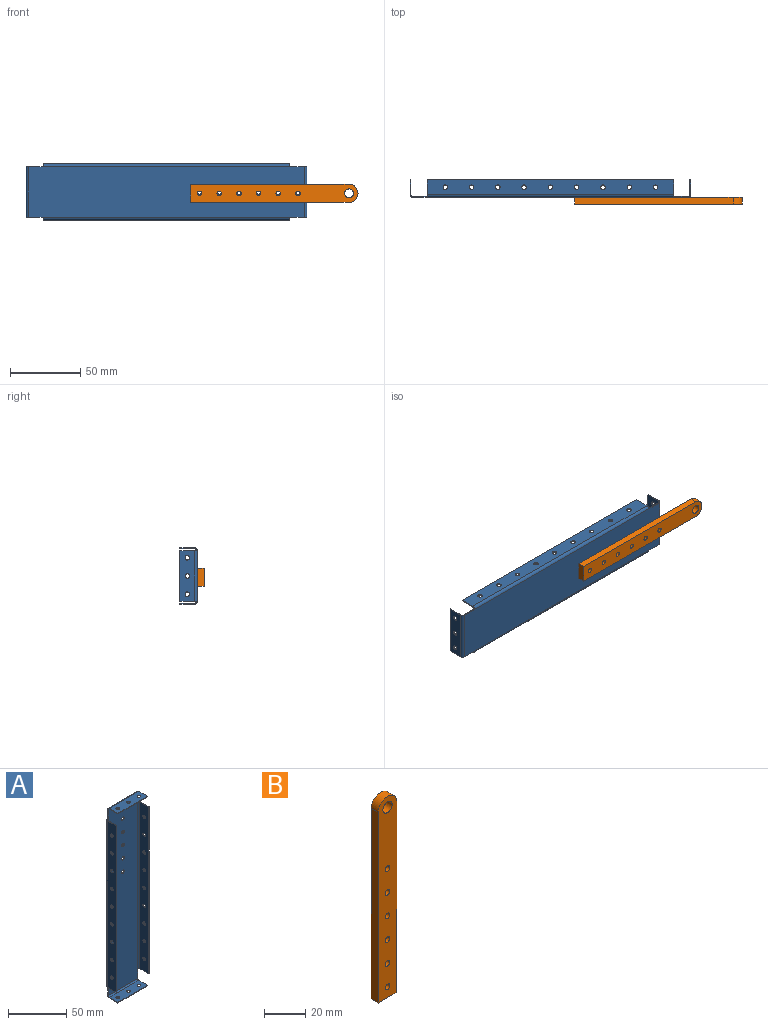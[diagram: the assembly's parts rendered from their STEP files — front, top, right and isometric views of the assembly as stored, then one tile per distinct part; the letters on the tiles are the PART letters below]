
ASSEMBLY  parts=2 mates=2
PART A: 76 faces, bbox 40x12.5x200 mm
  f0: plane 0.64x0mm, normal (0,0,-1), area 0mm2, adj f1,f73
  f1: plane 10.24x0.64mm, normal (1,0,0), area 6.6mm2, adj f0,f14,f15,f36
  f2: plane 10.24x0.64mm, normal (-1,0,0), area 6.6mm2, adj f3,f14,f15,f37
  f3: plane 0.64x0mm, normal (0,0,-1), area 0mm2, adj f2,f54
  f4: plane 0.64x0mm, normal (0,0,1), area 0mm2, adj f5,f55
  f5: plane 10.24x0.64mm, normal (-1,0,0), area 6.6mm2, adj f4,f14,f15,f24
  f6: plane 10.24x0.64mm, normal (1,0,0), area 6.6mm2, adj f8,f14,f15,f25
  f7: cylinder r=1.6mm len=3.2mm, axis (0,-1,0), area 6.4mm2, adj f14,f15
  f8: plane 0.64x0mm, normal (0,0,1), area 0mm2, adj f6,f72
  f9: cylinder r=1.6mm len=3.2mm, axis (0,-1,0), area 6.4mm2, adj f14,f15
  f10: cylinder r=1.6mm len=3.2mm, axis (0,-1,0), area 6.4mm2, adj f14,f15
  f11: cylinder r=1.6mm len=3.2mm, axis (0,-1,0), area 6.4mm2, adj f14,f15
  f12: cylinder r=1.6mm len=3.2mm, axis (0,-1,0), area 6.4mm2, adj f14,f15
  f13: cylinder r=1.6mm len=3.2mm, axis (0,-1,0), area 6.4mm2, adj f14,f15
  f14: plane 196.16x36.16mm, normal (0,1,0), area 7044.9mm2, adj f1,f2,f5,f6,f7,f9,f10,f11
  f15: plane 196.16x36.16mm, normal (0,-1,0), area 7044.9mm2, adj f1,f2,f5,f6,f7,f9,f10,f11
  f16: plane 10.58x0.64mm, normal (-1,0,0), area 6.8mm2, adj f17,f22,f23,f24
  f17: plane 36.16x0.64mm, normal (0,-1,0), area 23.1mm2, adj f16,f21,f22,f23
  f18: cylinder r=1.6mm len=3.2mm, axis (0,0,1), area 6.4mm2, adj f22,f23
  f19: cylinder r=1.6mm len=3.2mm, axis (0,0,1), area 6.4mm2, adj f22,f23
  f20: cylinder r=1.6mm len=3.2mm, axis (0,0,1), area 6.4mm2, adj f22,f23
  f21: plane 10.58x0.64mm, normal (1,0,0), area 6.8mm2, adj f17,f22,f23,f25
  f22: plane 36.16x10.58mm, normal (0,0,1), area 358.4mm2, adj f16,f17,f18,f19,f20,f21,f26
  f23: plane 36.16x10.58mm, normal (0,0,-1), area 358.4mm2, adj f16,f17,f18,f19,f20,f21,f27
  f24: plane 1.92x1.92mm, normal (-1,0,0), area 1.6mm2, adj f5,f16,f26,f27
  f25: plane 1.92x1.92mm, normal (1,0,0), area 1.6mm2, adj f6,f21,f26,f27
  f26: cylinder r=1.92mm len=36.16mm, axis (-1,0,0), area 109.1mm2, adj f14,f22,f24,f25
  f27: cylinder r=1.28mm len=36.16mm, axis (-1,0,0), area 72.7mm2, adj f15,f23,f24,f25
  f28: plane 36.16x0.64mm, normal (0,-1,0), area 23.1mm2, adj f29,f33,f34,f35
  f29: plane 10.58x0.64mm, normal (-1,0,0), area 6.8mm2, adj f28,f34,f35,f37
  f30: cylinder r=1.6mm len=3.2mm, axis (0,0,-1), area 6.4mm2, adj f34,f35
  f31: cylinder r=1.6mm len=3.2mm, axis (0,0,-1), area 6.4mm2, adj f34,f35
  f32: cylinder r=1.6mm len=3.2mm, axis (0,0,-1), area 6.4mm2, adj f34,f35
  f33: plane 10.58x0.64mm, normal (1,0,0), area 6.8mm2, adj f28,f34,f35,f36
  f34: plane 36.16x10.58mm, normal (0,0,-1), area 358.4mm2, adj f28,f29,f30,f31,f32,f33,f38
  f35: plane 36.16x10.58mm, normal (0,0,1), area 358.4mm2, adj f28,f29,f30,f31,f32,f33,f39
  f36: plane 1.92x1.92mm, normal (1,0,0), area 1.6mm2, adj f1,f33,f38,f39
  f37: plane 1.92x1.92mm, normal (-1,0,0), area 1.6mm2, adj f2,f29,f38,f39
  f38: cylinder r=1.92mm len=36.16mm, axis (1,0,0), area 109.1mm2, adj f14,f34,f36,f37
  f39: cylinder r=1.28mm len=36.16mm, axis (1,0,0), area 72.7mm2, adj f15,f35,f36,f37
  f40: plane 175.68x0.64mm, normal (0,-1,0), area 112.4mm2, adj f41,f51,f52,f53
  f41: plane 10.58x0.64mm, normal (0,0,1), area 6.8mm2, adj f40,f52,f53,f55
  f42: cylinder r=1.6mm len=3.2mm, axis (-1,0,0), area 6.4mm2, adj f52,f53
  f43: cylinder r=1.6mm len=3.2mm, axis (-1,0,0), area 6.4mm2, adj f52,f53
  f44: cylinder r=1.6mm len=3.2mm, axis (-1,0,0), area 6.4mm2, adj f52,f53
  f45: cylinder r=1.6mm len=3.2mm, axis (-1,0,0), area 6.4mm2, adj f52,f53
  f46: cylinder r=1.6mm len=3.2mm, axis (-1,0,0), area 6.4mm2, adj f52,f53
  f47: cylinder r=1.6mm len=3.2mm, axis (-1,0,0), area 6.4mm2, adj f52,f53
  f48: cylinder r=1.6mm len=3.2mm, axis (-1,0,0), area 6.4mm2, adj f52,f53
  f49: cylinder r=1.6mm len=3.2mm, axis (-1,0,0), area 6.4mm2, adj f52,f53
  f50: cylinder r=1.6mm len=3.2mm, axis (-1,0,0), area 6.4mm2, adj f52,f53
  f51: plane 10.58x0.64mm, normal (0,0,-1), area 6.8mm2, adj f40,f52,f53,f54
  f52: plane 175.68x10.58mm, normal (-1,0,0), area 1786.3mm2, adj f40,f41,f42,f43,f44,f45,f46,f47
  f53: plane 175.68x10.58mm, normal (1,0,0), area 1786.3mm2, adj f40,f41,f42,f43,f44,f45,f46,f47
  f54: plane 1.92x1.92mm, normal (0,0,-1), area 1.6mm2, adj f3,f51,f56,f57
  f55: plane 1.92x1.92mm, normal (0,0,1), area 1.6mm2, adj f4,f41,f56,f57
  f56: cylinder r=1.92mm len=175.68mm, axis (0,0,-1), area 529.8mm2, adj f14,f52,f54,f55
  f57: cylinder r=1.28mm len=175.68mm, axis (0,0,-1), area 353.2mm2, adj f15,f53,f54,f55
  f58: plane 175.68x0.64mm, normal (0,-1,0), area 112.4mm2, adj f59,f69,f70,f71
  f59: plane 10.58x0.64mm, normal (0,0,-1), area 6.8mm2, adj f58,f70,f71,f73
  f60: cylinder r=1.6mm len=3.2mm, axis (1,0,0), area 6.4mm2, adj f70,f71
  f61: cylinder r=1.6mm len=3.2mm, axis (1,0,0), area 6.4mm2, adj f70,f71
  f62: cylinder r=1.6mm len=3.2mm, axis (1,0,0), area 6.4mm2, adj f70,f71
  f63: cylinder r=1.6mm len=3.2mm, axis (1,0,0), area 6.4mm2, adj f70,f71
  f64: cylinder r=1.6mm len=3.2mm, axis (1,0,0), area 6.4mm2, adj f70,f71
  f65: cylinder r=1.6mm len=3.2mm, axis (1,0,0), area 6.4mm2, adj f70,f71
  f66: cylinder r=1.6mm len=3.2mm, axis (1,0,0), area 6.4mm2, adj f70,f71
  f67: cylinder r=1.6mm len=3.2mm, axis (1,0,0), area 6.4mm2, adj f70,f71
  f68: cylinder r=1.6mm len=3.2mm, axis (1,0,0), area 6.4mm2, adj f70,f71
  f69: plane 10.58x0.64mm, normal (0,0,1), area 6.8mm2, adj f58,f70,f71,f72
  f70: plane 175.68x10.58mm, normal (1,0,0), area 1786.3mm2, adj f58,f59,f60,f61,f62,f63,f64,f65
  f71: plane 175.68x10.58mm, normal (-1,0,0), area 1786.3mm2, adj f58,f59,f60,f61,f62,f63,f64,f65
  f72: plane 1.92x1.92mm, normal (0,0,1), area 1.6mm2, adj f8,f69,f74,f75
  f73: plane 1.92x1.92mm, normal (0,0,-1), area 1.6mm2, adj f0,f59,f74,f75
  f74: cylinder r=1.92mm len=175.68mm, axis (0,0,1), area 529.8mm2, adj f14,f70,f72,f73
  f75: cylinder r=1.28mm len=175.68mm, axis (0,0,1), area 353.2mm2, adj f15,f71,f72,f73
PART B: 13 faces, bbox 12.8x4.8x119.2 mm
  f0: cylinder r=6.4mm len=12.8mm, axis (0,1,0), area 97.1mm2, adj f1,f10,f11,f12
  f1: plane 112.8x4.83mm, normal (-1,0,0), area 544.8mm2, adj f0,f2,f11,f12
  f2: plane 12.8x4.83mm, normal (0,0,-1), area 61.8mm2, adj f1,f10,f11,f12
  f3: cylinder r=3.17mm len=6.35mm, axis (0,1,0), area 96.4mm2, adj f11,f12
  f4: cylinder r=1.6mm len=4.83mm, axis (0,1,0), area 48.6mm2, adj f11,f12
  f5: cylinder r=1.6mm len=4.83mm, axis (0,1,0), area 48.6mm2, adj f11,f12
  f6: cylinder r=1.6mm len=4.83mm, axis (0,1,0), area 48.6mm2, adj f11,f12
  f7: cylinder r=1.6mm len=4.83mm, axis (0,1,0), area 48.6mm2, adj f11,f12
  f8: cylinder r=1.6mm len=4.83mm, axis (0,1,0), area 48.6mm2, adj f11,f12
  f9: cylinder r=1.6mm len=4.83mm, axis (0,1,0), area 48.6mm2, adj f11,f12
  f10: plane 112.8x4.83mm, normal (1,0,0), area 544.8mm2, adj f0,f2,f11,f12
  f11: plane 119.2x12.8mm, normal (0,-1,0), area 1428.3mm2, adj f0,f1,f2,f3,f4,f5,f6,f7
  f12: plane 119.2x12.8mm, normal (0,1,0), area 1428.3mm2, adj f0,f1,f2,f3,f4,f5,f6,f7
PLACE A rot(axis=(-0.71,0,-0.71),180deg) t=(82.03,11.44,9.61)mm
PLACE B rot(axis=(-0.71,0,-0.71),180deg) t=(212.03,6.61,8.63)mm
MATE pin_slot A.f7 <-> B.f9  axis (0,-1,0) through (175.63,11.44,9.61)mm
MATE pin_slot B.f8 <-> A.f9  axis (0,1,0) through (161.63,11.44,8.63)mm
